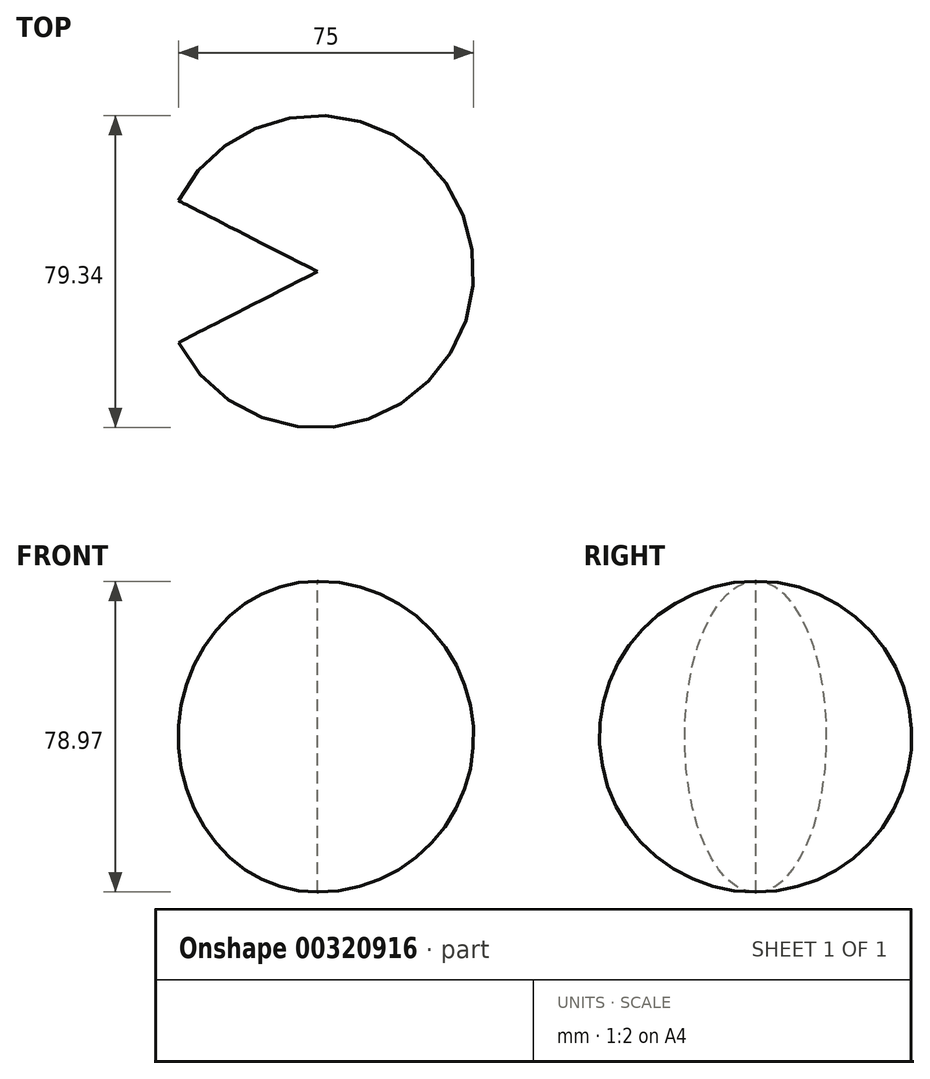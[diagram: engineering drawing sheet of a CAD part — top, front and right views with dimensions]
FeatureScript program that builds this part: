
annotation { "Feature Type Name" : "Feature", "Feature Type Description" : "" }
export const myFeature = defineFeature(function(context is Context, id is Id, definition is map)
    precondition{}
    {
        {
            var Q0;
            Q0=qCreatedBy(makeId("Front.planeOp"),FACE);
            var sketch = newSketch(context, id + "F0", { "sketchPlane" : qUnion([Q0])});
            skLineSegment(sketch, "E0", {"start": v(0, -27.55) * mm, "end": v(0, 51.42) * mm});
            skArc(sketch, "E1", {"start": v(0, -27.55) * mm, "mid": v(39.67, 11.93) * mm, "end": v(0, 51.42) * mm});
            skSolve(sketch);
        }
        {
            var Q0;
            Q0 = qSketchRegion(id + "F0", true);
            var Q1;
            Q1=sQuery(id+"F0.wireOp",EDGE,"E0");
            revolve(context, id + "F1", {"entities" : qUnion([Q0]), "axis" : qUnion([Q1]), "revolveType" : RevolveType.SYMMETRIC, "angle" : 305.9 * degree});
        }
    });
